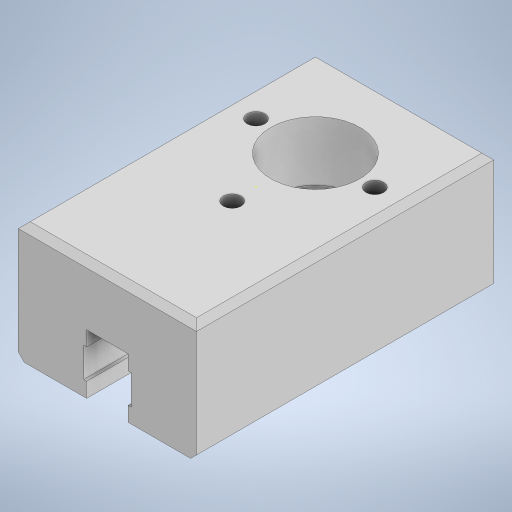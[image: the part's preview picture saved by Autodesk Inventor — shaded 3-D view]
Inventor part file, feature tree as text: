
AUTODESK INVENTOR PART (.ipt)
format: ipt  version: 2023.2 (Build 272271030, 271C)  size: 338,944 bytes
history: native  units: mm
features: sketch x9, chamfer x6, extrude x5, hole x3
ambient origin geometry x8: Origin, YZ Plane, XZ Plane, XY Plane, X Axis, Y Axis, Z Axis, Center Point
bodies: Solid1 (feature_tree)
feature tree (23):
  extrude  "Extrusion1"  Depth=100.0mm
  extrude  "Extrusion2"  Depth=6.0mm
  extrude  "Extrusion3"  Depth=10.0mm
  extrude  "Extrusion4"  Depth=6.0mm
  hole  "Hole1"  [1 undecoded]
  chamfer  "Chamfer1"  Distance=20.0mm
  chamfer  "Chamfer2"  Distance=5.0mm
  chamfer  "Chamfer3"  Distance=22.0mm
  chamfer  "Chamfer4"  Distance=10.0mm
  chamfer  "Chamfer5"  Distance=23.0mm
  chamfer  "Chamfer6"  Distance=23.0mm
  hole  "Hole2"  [1 undecoded]
  sketch  "Sketch7"  dims[d15=23.0mm]
  extrude  "Extrusion5"  Depth=5.0mm TaperAngle=0.0deg
  hole  "Hole3"  [1 undecoded]
  sketch  "Sketch1"  dims[d0=60.0mm d1=100.0mm]
  sketch  "Sketch2"  dims[d2=6.0mm d3=6.0mm]
  sketch  "Sketch3"  dims[d5=58.0mm d6=10.0mm]
  sketch  "Sketch4"  dims[d8=30.0mm d9=6.0mm]
  sketch  "Sketch5"  dims[d10=10.0mm d11=30.0mm]
  sketch  "Sketch6"  dims[d12=30.0mm d13=20.0mm d14=0.0mm]
  sketch  "Sketch8"  dims[d16=23.0mm d17=5.0mm d18=0.0mm]
  sketch  "Sketch9"  dims[d19=22.0mm d20=22.0mm d21=10.0mm d22=0.0mm d23=23.0mm d25=23.0mm d26=100.0mm d27=5.0mm d28=0.0mm d29=6.0mm d30=6.0mm d31=6.0mm d32=6.0mm d33=6.0mm d34=6.0mm d35=15.0mm d36=35.0mm d37=70.0mm d38=13.0mm d39=13.0mm d40=6.0mm d41=6.0mm d42=4.0mm d43=2.0mm d44=90.0deg d45=9.0mm d46=20.594885mm d47=2.0mm d48=2.0mm d49=45.0deg d50=2.0mm d51=2.0mm d52=45.0deg d53=2.0mm d54=2.0mm d55=45.0deg d56=2.0mm d57=2.0mm d58=45.0deg d59=2.0mm d60=2.0mm d61=45.0deg d62=2.0mm d63=2.0mm d64=45.0deg d65=8.0mm d66=8.0mm d67=20.0mm d68=20.0mm d69=10.0mm d70=8.0mm d71=6.0mm d72=4.0mm d73=2.0mm d74=90.0deg d75=12.0mm d76=20.594885mm d77=0.01mm d78=0.0mm d79=6.0mm d80=58.0mm d81=6.0mm d82=6.0mm d83=4.0mm d84=2.0mm d85=90.0deg d86=10.0mm d87=20.594885mm]
note: 3 required parameter values undecoded (feature->parameter linkage not recoverable at this tier; creation-order binding heuristic only, values carry confidence <= 0.55)
